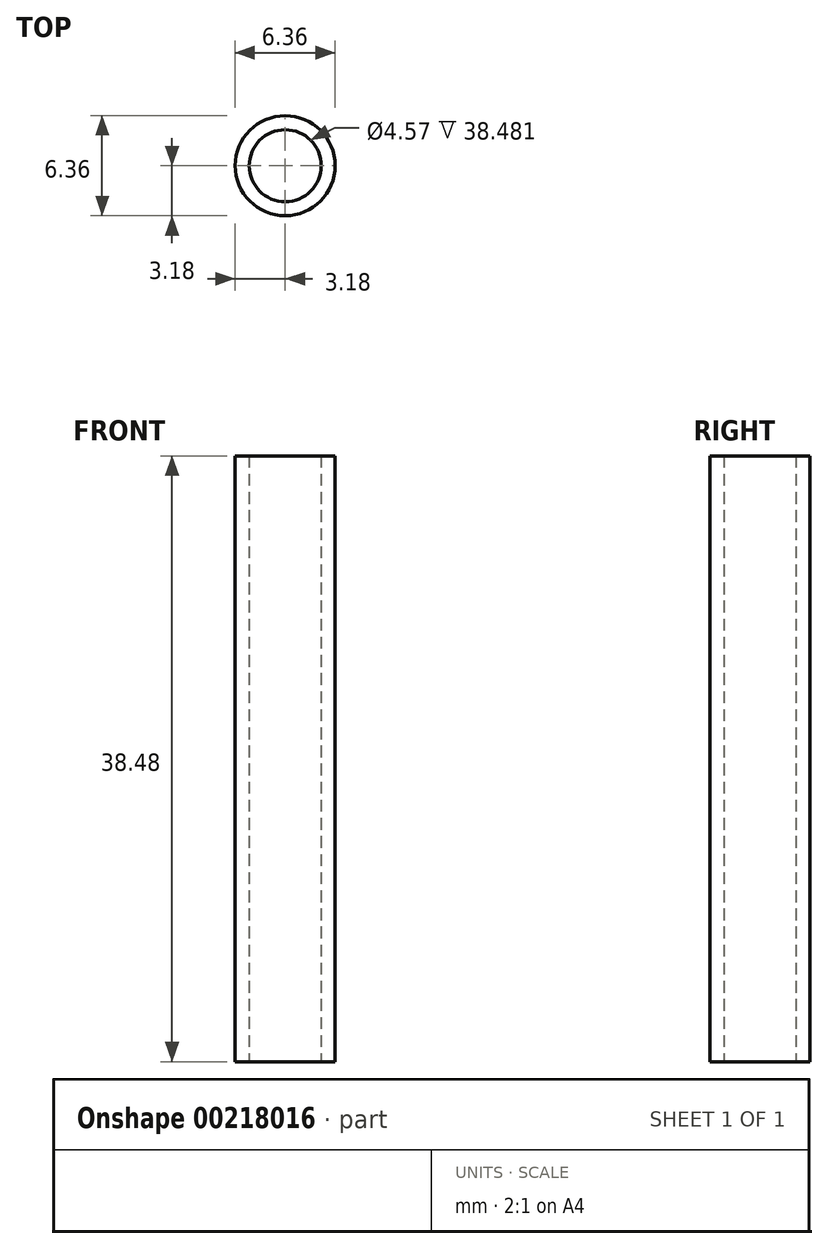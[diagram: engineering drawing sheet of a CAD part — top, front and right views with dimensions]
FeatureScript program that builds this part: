
annotation { "Feature Type Name" : "Feature", "Feature Type Description" : "" }
export const myFeature = defineFeature(function(context is Context, id is Id, definition is map)
    precondition{}
    {
        {
            var Q0;
            Q0=qCreatedBy(makeId("Top.planeOp"),FACE);
            var sketch = newSketch(context, id + "F0", { "sketchPlane" : qUnion([Q0])});
            skCircle(sketch, "E0", {"center": v(0, 0) * mm, "radius": 3.18 * mm});
            skCircle(sketch, "E1", {"center": v(0, 0) * mm, "radius": 2.29 * mm});
            skSolve(sketch);
        }
        {
            var Q0;
            Q0 = qSketchRegion(id + "F0", true);
            extrude(context, id + "F1", {"entities" : qUnion([Q0]), "depth" : 38.48 * mm, "offsetDistance" : 25.4 * mm});
        }
    });
